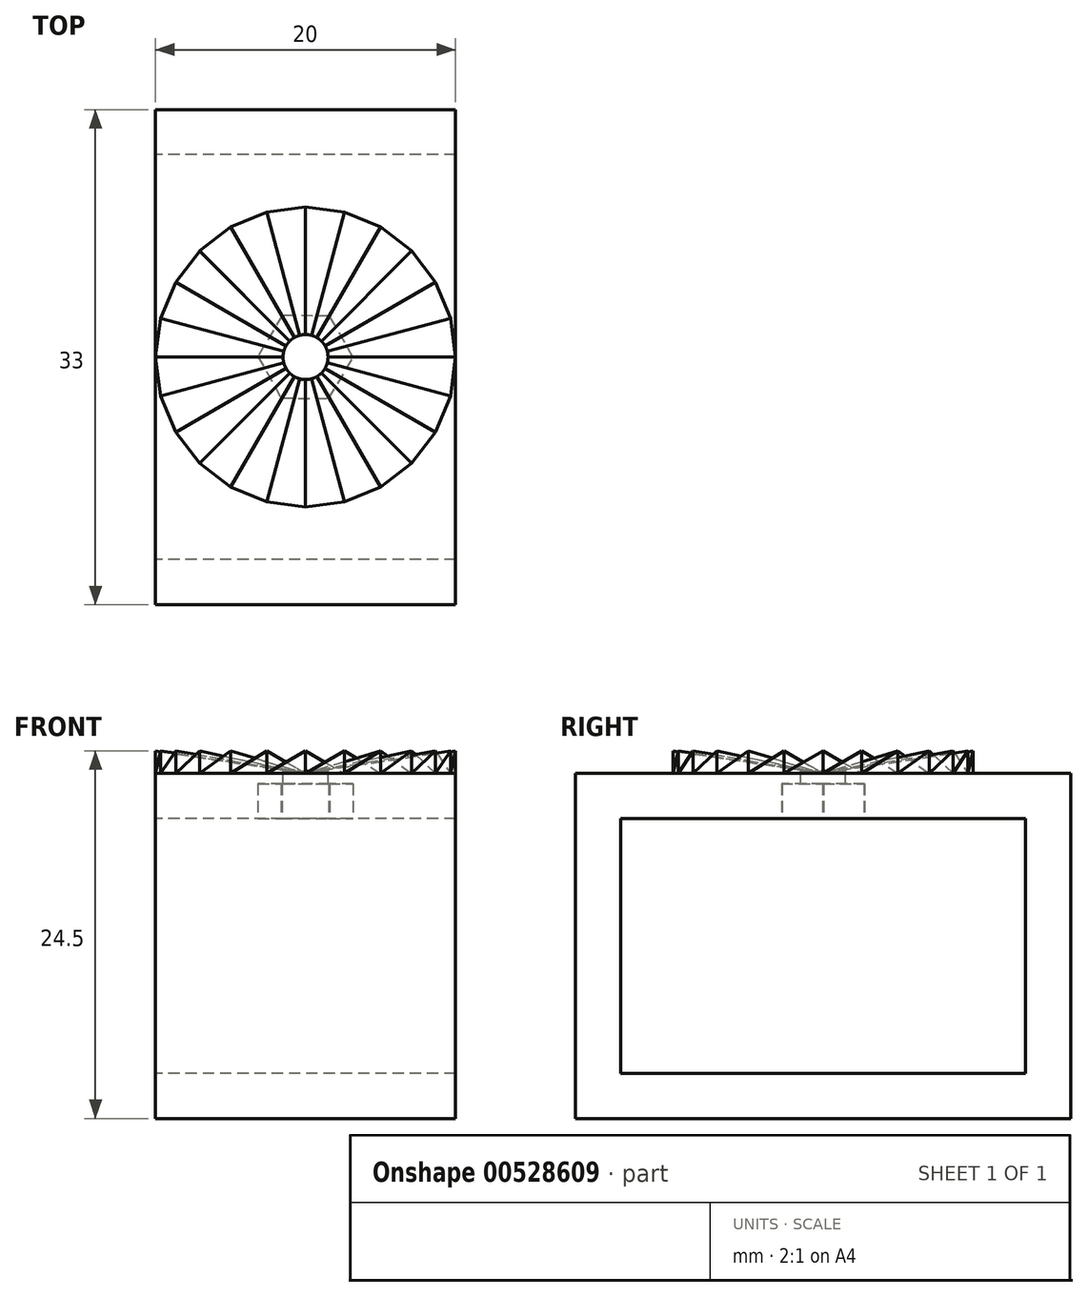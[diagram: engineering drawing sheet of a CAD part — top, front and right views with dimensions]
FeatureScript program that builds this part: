
annotation { "Feature Type Name" : "Feature", "Feature Type Description" : "" }
export const myFeature = defineFeature(function(context is Context, id is Id, definition is map)
    precondition{}
    {
        {
            var Q0;
            Q0=qCreatedBy(makeId("Top.planeOp"),FACE);
            var sketch = newSketch(context, id + "F0", { "sketchPlane" : qUnion([Q0])});
            skCircle(sketch, "E0", {"center": v(0, 0) * mm, "radius": 10 * mm});
            skLineSegment(sketch, "E1", {"start": v(0, 0) * mm, "end": v(0, 10) * mm});
            skLineSegment(sketch, "E2", {"start": v(0, 0) * mm, "end": v(2.59, 9.66) * mm});
            skLineSegment(sketch, "E3", {"start": v(0, 10) * mm, "end": v(2.59, 9.66) * mm});
            skCircle(sketch, "E4", {"center": v(0, 0) * mm, "radius": 1.5 * mm});
            skSolve(sketch);
        }
        {
            var Q0;
            Q0=sQuery(id+"F0.wireOp",EDGE,"E3");
            cPlane(context, id + "F1", {"entities" : qUnion([Q0]), "cplaneType" : CPlaneType.LINE_ANGLE, "offset" : 25 * mm, "angle" : 0 * degree, "width" : 150 * mm, "height" : 150 * mm});
        }
        {
            var Q0;
            Q0=qCreatedBy(id+"F1.planeOp",FACE);
            var sketch = newSketch(context, id + "F2", { "sketchPlane" : qUnion([Q0])});
            skLineSegment(sketch, "E5", {"start": v(1.3, 0) * mm, "end": v(1.3, 1.5) * mm});
            skLineSegment(sketch, "E6", {"start": v(1.3, 1.5) * mm, "end": v(-1.3, 0) * mm});
            skLineSegment(sketch, "E7", {"start": v(-1.3, 0) * mm, "end": v(1.3, 0) * mm});
            skLineSegment(sketch, "E8", {"start": v(-1.3, 0) * mm, "end": v(-1.3, 1.5) * mm});
            skLineSegment(sketch, "E9", {"start": v(-1.3, 1.5) * mm, "end": v(1.3, 1.5) * mm});
            skSolve(sketch);
        }
        {
            var Q0;
            Q0=makeQuery(id+"F2.imprint","IMPRINT",FACE,{"disambiguationData":[TD([[makeQuery(id+"F2.imprint","IMPRINT",EDGE,{"derivedFrom":sQuery(id+"F2.wireOp",EDGE,"E5")}),1.0]])]});
            var Q1;
            Q1=sQuery(id+"F0.wireOp",VERTEX,"E0.center");
            loft(context, id + "F3", {"sheetProfilesArray" : [{ "sheetProfileEntities" : qUnion([Q0]) }, { "sheetProfileEntities" : qUnion([Q1]) }]});
        }
        {
            var Q0;
            Q0=qCreatedBy(makeId("Right.planeOp"),FACE);
            var sketch = newSketch(context, id + "F4", { "sketchPlane" : qUnion([Q0])});
            skLineSegment(sketch, "E10", {"start": v(0, -4.83) * mm, "end": v(0, 8.7) * mm, "construction": true});
            skSolve(sketch);
        }
        {
            var Q0;
            Q0=makeQuery(id+"F3.opLoft","SWEPT_BODY",BODY,{"disambiguationData":[OSD([sQuery(id+"F0.wireOp",VERTEX,"E0.center"),makeQuery(id+"F2.imprint","IMPRINT",FACE,{"disambiguationData":[TD([[makeQuery(id+"F2.imprint","IMPRINT",EDGE,{"derivedFrom":sQuery(id+"F2.wireOp",EDGE,"E5")}),1.0]])]})])]});
            var Q1;
            Q1=sQuery(id+"F4.wireOp",EDGE,"E10");
            circularPattern(context, id + "F5", {"entities" : qUnion([Q0]), "axis" : qUnion([Q1]), "angle" : 360 * degree, "instanceCount" : 24, "equalSpace" : true});
        }
        {
            var Q0;
            Q0=qCreatedBy(makeId("Right.planeOp"),FACE);
            var sketch = newSketch(context, id + "F6", { "sketchPlane" : qUnion([Q0])});
            skLineSegment(sketch, "E11", {"start": v(0, 0) * mm, "end": v(-16.5, 0) * mm, "construction": true});
            skLineSegment(sketch, "E12.bottom", {"start": v(-16.5, 0) * mm, "end": v(16.5, 0) * mm});
            skLineSegment(sketch, "E12.top", {"start": v(-16.5, -23) * mm, "end": v(16.5, -23) * mm});
            skLineSegment(sketch, "E12.left", {"start": v(-16.5, 0) * mm, "end": v(-16.5, -23) * mm});
            skLineSegment(sketch, "E12.right", {"start": v(16.5, 0) * mm, "end": v(16.5, -23) * mm});
            skLineSegment(sketch, "E13.0", {"start": v(-13.5, -3) * mm, "end": v(-13.5, -20) * mm});
            skLineSegment(sketch, "E13.1", {"start": v(-13.5, -3) * mm, "end": v(13.5, -3) * mm});
            skLineSegment(sketch, "E13.2", {"start": v(13.5, -3) * mm, "end": v(13.5, -20) * mm});
            skLineSegment(sketch, "E13.3", {"start": v(-13.5, -20) * mm, "end": v(13.5, -20) * mm});
            skSolve(sketch);
        }
        {
            var Q0;
            Q0=makeQuery(id+"F6.imprint","IMPRINT",FACE,{"disambiguationData":[TD([[makeQuery(id+"F6.imprint","IMPRINT",EDGE,{"derivedFrom":sQuery(id+"F6.wireOp",EDGE,"E12.bottom")}),-1.0]])]});
            extrude(context, id + "F7", {"entities" : qUnion([Q0]), "depth" : 10 * mm, "offsetDistance" : 25 * mm, "hasSecondDirection" : true, "secondDirectionOppositeDirection" : true, "secondDirectionDepth" : 10 * mm});
        }
        {
            var Q0;
            {var subQ0=sQuery(id+"F0.wireOp",EDGE,"E2");var subQ1=sQuery(id+"F0.wireOp",EDGE,"E1");var subQ2=makeQuery(id+"F0.imprint","INTERSECT",VERTEX,{"derivedFrom":[subQ1,subQ0]});Q0=makeQuery(id+"F0.imprint","IMPRINT",FACE,{"disambiguationData":[TD([[makeQuery(id+"F0.imprint","IMPRINT",EDGE,{"disambiguationData":[TD([[subQ2,-1.0]])],"derivedFrom":subQ1}),1.0]])]});}
            var Q1;
            {var subQ0=sQuery(id+"F0.wireOp",EDGE,"E2");var subQ1=sQuery(id+"F0.wireOp",EDGE,"E1");var subQ2=makeQuery(id+"F0.imprint","INTERSECT",VERTEX,{"derivedFrom":[subQ1,subQ0]});Q1=makeQuery(id+"F0.imprint","IMPRINT",FACE,{"disambiguationData":[TD([[makeQuery(id+"F0.imprint","IMPRINT",EDGE,{"disambiguationData":[TD([[subQ2,-1.0]])],"derivedFrom":subQ1}),-1.0]])]});}
            extrude(context, id + "F8", {"entities" : qUnion([Q0, Q1]), "operationType" : NewBodyOperationType.REMOVE, "oppositeDirection" : true, "depth" : 3 * mm, "offsetDistance" : 25 * mm, "hasSecondDirection" : true, "secondDirectionOppositeDirection" : false, "secondDirectionDepth" : 5 * mm});
        }
        {
            var Q0;
            Q0=makeQuery(id+"F7.opExtrude","SWEPT_FACE",FACE,{"disambiguationData":[OSD([sQuery(id+"F6.wireOp",EDGE,"E13.1")])]});
            var sketch = newSketch(context, id + "F9", { "sketchPlane" : qUnion([Q0])});
            skCircle(sketch, "E14.cCircle", {"center": v(0, 0) * mm, "radius": 2.75 * mm, "construction": true});
            skLineSegment(sketch, "E14.0", {"start": v(-1.55, -2.77) * mm, "end": v(-3.18, -0.04) * mm});
            skLineSegment(sketch, "E14.1", {"start": v(-3.18, -0.04) * mm, "end": v(-1.62, 2.73) * mm});
            skLineSegment(sketch, "E14.2", {"start": v(-1.62, 2.73) * mm, "end": v(1.55, 2.77) * mm});
            skLineSegment(sketch, "E14.3", {"start": v(1.55, 2.77) * mm, "end": v(3.18, 0.04) * mm});
            skLineSegment(sketch, "E14.4", {"start": v(3.18, 0.04) * mm, "end": v(1.62, -2.73) * mm});
            skLineSegment(sketch, "E14.5", {"start": v(1.62, -2.73) * mm, "end": v(-1.55, -2.77) * mm});
            skPoint(sketch, "E14.0.midPoint", {"position": v(-2.36, -1.4) * mm});
            skSolve(sketch);
        }
        {
            var Q0;
            Q0 = qSketchRegion(id + "F9", true);
            extrude(context, id + "F10", {"entities" : qUnion([Q0]), "operationType" : NewBodyOperationType.REMOVE, "oppositeDirection" : true, "depth" : 2.3 * mm, "offsetDistance" : 25 * mm});
        }
    });
